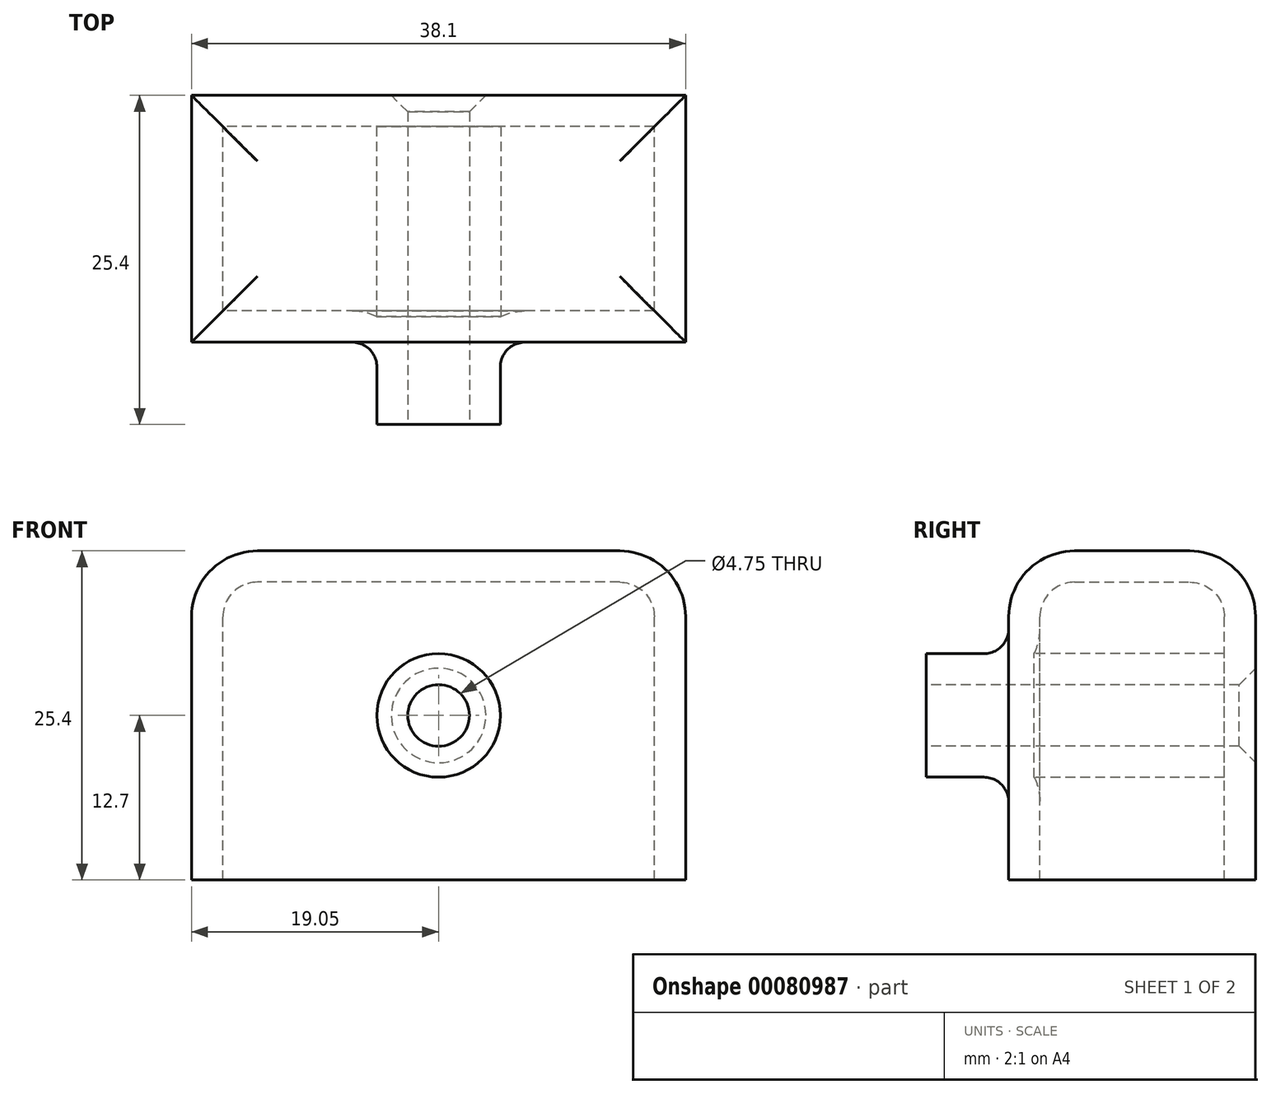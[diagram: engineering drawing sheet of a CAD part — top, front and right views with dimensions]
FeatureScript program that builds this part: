
annotation { "Feature Type Name" : "Feature", "Feature Type Description" : "" }
export const myFeature = defineFeature(function(context is Context, id is Id, definition is map)
    precondition{}
    {
        {
            var Q0;
            Q0=qCreatedBy(makeId("Front.planeOp"),FACE);
            var sketch = newSketch(context, id + "F0", { "sketchPlane" : qUnion([Q0])});
            skLineSegment(sketch, "E0.bottom", {"start": v(0, 0) * mm, "end": v(-38.1, 0) * mm});
            skLineSegment(sketch, "E0.top", {"start": v(0, 25.4) * mm, "end": v(-38.1, 25.4) * mm});
            skLineSegment(sketch, "E0.left", {"start": v(0, 0) * mm, "end": v(0, 25.4) * mm});
            skLineSegment(sketch, "E0.right", {"start": v(-38.1, 0) * mm, "end": v(-38.1, 25.4) * mm});
            skSolve(sketch);
        }
        {
            var Q0;
            Q0 = qSketchRegion(id + "F0", true);
            extrude(context, id + "F1", {"entities" : qUnion([Q0]), "depth" : 19.05 * mm});
        }
        {
            var Q0;
            Q0=qCreatedBy(makeId("Front.planeOp"),FACE);
            var sketch = newSketch(context, id + "F2", { "sketchPlane" : qUnion([Q0])});
            skCircle(sketch, "E1", {"center": v(-19.05, 12.7) * mm, "radius": 4.76 * mm});
            skSolve(sketch);
        }
        {
            var Q0;
            Q0 = qSketchRegion(id + "F2", true);
            extrude(context, id + "F3", {"entities" : qUnion([Q0]), "operationType" : NewBodyOperationType.ADD, "depth" : 25.4 * mm});
        }
        {
            var Q0;
            Q0=makeQuery(id+"F3.opExtrude","CAP_FACE",FACE,{"disambiguationData":[OSD([sQuery(id+"F2.wireOp",EDGE,"E1")])],"isStart":false});
            var sketch = newSketch(context, id + "F4", { "sketchPlane" : qUnion([Q0])});
            skCircle(sketch, "E2", {"center": v(-19.05, 12.7) * mm, "radius": 2.37 * mm});
            skSolve(sketch);
        }
        {
            var Q0;
            Q0 = qSketchRegion(id + "F4", true);
            extrude(context, id + "F5", {"entities" : qUnion([Q0]), "operationType" : NewBodyOperationType.REMOVE, "endBound" : BoundingType.THROUGH_ALL, "oppositeDirection" : true, "depth" : 25.4 * mm});
        }
        {
            var Q0;
            Q0=makeQuery(id+"F1.opExtrude","SWEPT_EDGE",EDGE,{"disambiguationData":[OSD([sQuery(id+"F0.wireOp",EDGE,"E0.top"),sQuery(id+"F0.wireOp",EDGE,"E0.right")])]});
            var Q1;
            Q1=makeQuery(id+"F1.opExtrude","CAP_EDGE",EDGE,{"disambiguationData":[OSD([sQuery(id+"F0.wireOp",EDGE,"E0.top")])],"isStart":true});
            var Q2;
            Q2=makeQuery(id+"F1.opExtrude","SWEPT_EDGE",EDGE,{"disambiguationData":[OSD([sQuery(id+"F0.wireOp",EDGE,"E0.top"),sQuery(id+"F0.wireOp",EDGE,"E0.left")])]});
            var Q3;
            Q3=makeQuery(id+"F1.opExtrude","CAP_EDGE",EDGE,{"disambiguationData":[OSD([sQuery(id+"F0.wireOp",EDGE,"E0.top")])],"isStart":false});
            fillet(context, id + "F6", {"entities" : qUnion([Q0, Q1, Q2, Q3]), "radius" : 5.08 * mm, "tangentPropagation" : true, "allowEdgeOverflow" : false});
        }
        {
            var Q0;
            Q0=makeQuery(id+"F5.boolean.opBoolean","INTERSECT",EDGE,{"derivedFrom":[makeQuery(id+"F1.opExtrude","CAP_FACE",FACE,{"disambiguationData":[OSD([sQuery(id+"F0.wireOp",EDGE,"E0.bottom"),sQuery(id+"F0.wireOp",EDGE,"E0.top"),sQuery(id+"F0.wireOp",EDGE,"E0.left"),sQuery(id+"F0.wireOp",EDGE,"E0.right")])],"isStart":true}),makeQuery(id+"F5.opExtrude","SWEPT_FACE",FACE,{"disambiguationData":[OSD([sQuery(id+"F4.wireOp",EDGE,"E2")])]})]});
            chamfer(context, id + "F7", {"entities" : qUnion([Q0]), "width" : 1.27 * mm, "tangentPropagation" : true});
        }
        {
            var Q0;
            Q0=makeQuery(id+"F3.boolean.opBoolean","INTERSECT",EDGE,{"derivedFrom":[makeQuery(id+"F1.opExtrude","CAP_FACE",FACE,{"disambiguationData":[OSD([sQuery(id+"F0.wireOp",EDGE,"E0.bottom"),sQuery(id+"F0.wireOp",EDGE,"E0.top"),sQuery(id+"F0.wireOp",EDGE,"E0.left"),sQuery(id+"F0.wireOp",EDGE,"E0.right")])],"isStart":false}),makeQuery(id+"F3.opExtrude","SWEPT_FACE",FACE,{"disambiguationData":[OSD([sQuery(id+"F2.wireOp",EDGE,"E1")])]})]});
            fillet(context, id + "F8", {"entities" : qUnion([Q0]), "radius" : 1.9 * mm, "tangentPropagation" : true, "allowEdgeOverflow" : false});
        }
        {
            var Q0;
            Q0=makeQuery(id+"F1.opExtrude","SWEPT_FACE",FACE,{"disambiguationData":[OSD([sQuery(id+"F0.wireOp",EDGE,"E0.bottom")])]});
            shell(context, id + "F9", {"entities" : qUnion([Q0]), "thickness" : 2.41 * mm});
        }
    });
